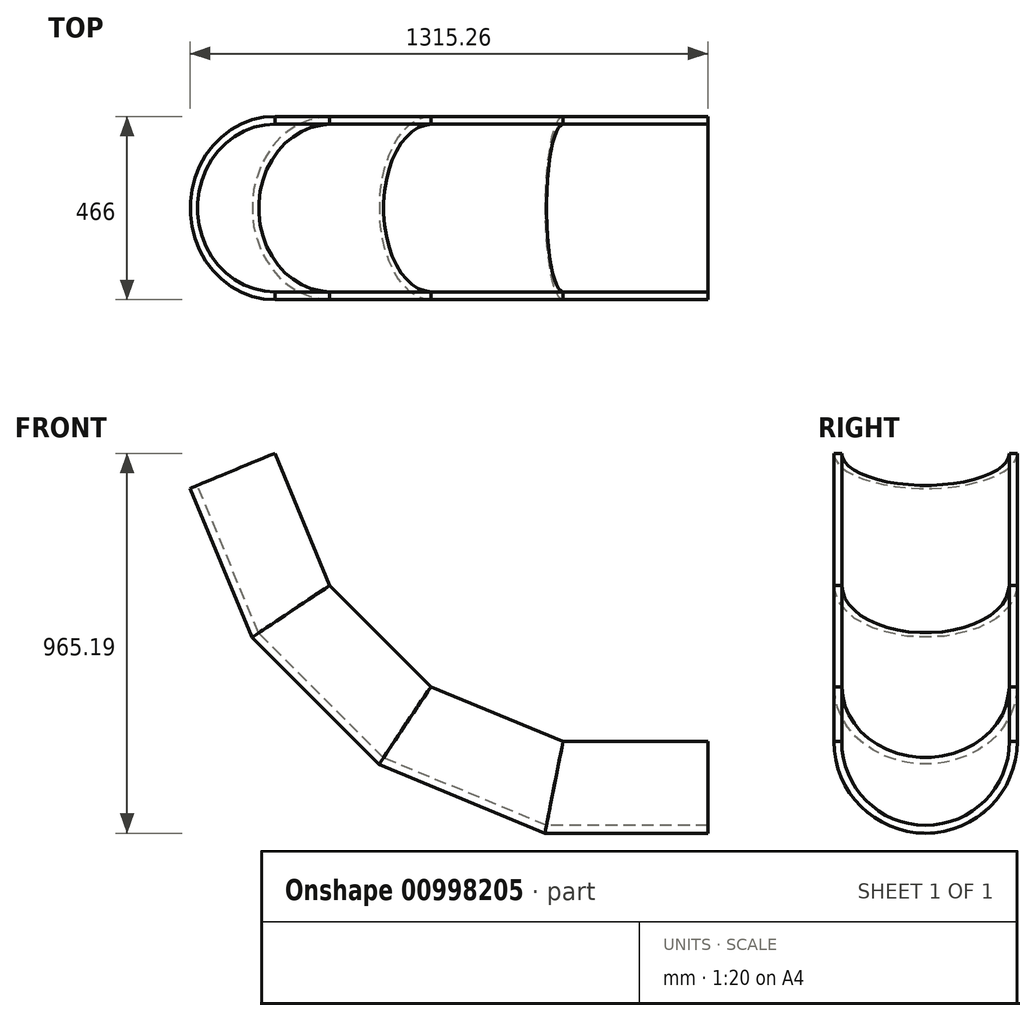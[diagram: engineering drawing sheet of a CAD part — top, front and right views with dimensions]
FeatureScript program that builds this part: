
annotation { "Feature Type Name" : "Feature", "Feature Type Description" : "" }
export const myFeature = defineFeature(function(context is Context, id is Id, definition is map)
    precondition{}
    {
        {
            var Q0;
            Q0=qCreatedBy(makeId("Front.planeOp"),FACE);
            var sketch = newSketch(context, id + "F0", { "sketchPlane" : qUnion([Q0])});
            skLineSegment(sketch, "E0", {"start": v(0, 0) * mm, "end": v(0, -183.8) * mm, "construction": true});
            skLineSegment(sketch, "E1", {"start": v(0, -183.8) * mm, "end": v(139.15, -519.74) * mm});
            skLineSegment(sketch, "E2", {"start": v(139.15, -519.74) * mm, "end": v(396.26, -776.85) * mm});
            skLineSegment(sketch, "E3", {"start": v(396.26, -776.85) * mm, "end": v(732.2, -916) * mm});
            skLineSegment(sketch, "E4", {"start": v(732.2, -916) * mm, "end": v(1100, -916) * mm});
            skLineSegment(sketch, "E5", {"start": v(69.57, -351.77) * mm, "end": v(914, -2) * mm, "construction": true});
            skLineSegment(sketch, "E6", {"start": v(914, -2) * mm, "end": v(267.7, -648.3) * mm, "construction": true});
            skLineSegment(sketch, "E7", {"start": v(914, -2) * mm, "end": v(564.23, -846.43) * mm, "construction": true});
            skLineSegment(sketch, "E8", {"start": v(914, -2) * mm, "end": v(0, -2) * mm, "construction": true});
            skSolve(sketch);
        }
        {
            var Q0;
            Q0=sQuery(id+"F0.wireOp",VERTEX,"E4.end");
            var Q1;
            Q1=sQuery(id+"F0.wireOp",EDGE,"E4");
            cPlane(context, id + "F1", {"entities" : qUnion([Q0, Q1]), "cplaneType" : CPlaneType.LINE_POINT, "offset" : 25 * mm, "width" : 150 * mm, "height" : 150 * mm});
        }
        {
            var Q0;
            Q0=qCreatedBy(id+"F1.planeOp",FACE);
            var sketch = newSketch(context, id + "F2", { "sketchPlane" : qUnion([Q0])});
            skArc(sketch, "E9", {"start": v(-213, -916) * mm, "mid": v(0, -1129) * mm, "end": v(213, -916) * mm});
            skArc(sketch, "E10", {"start": v(-233, -916) * mm, "mid": v(0, -1149) * mm, "end": v(233, -916) * mm});
            skLineSegment(sketch, "E11", {"start": v(-213, -916) * mm, "end": v(-233, -916) * mm});
            skLineSegment(sketch, "E12", {"start": v(213, -916) * mm, "end": v(233, -916) * mm});
            skSolve(sketch);
        }
        {
            var Q0;
            Q0 = qSketchRegion(id + "F2", true);
            var Q1;
            Q1 = qConstructionFilter(qBodyType(qCreatedBy(id + "F0" ,EDGE), BodyType.WIRE), ConstructionObject.NO);
            sweep(context, id + "F3", {"profiles" : qUnion([Q0]), "path" : qUnion([Q1])});
        }
    });
